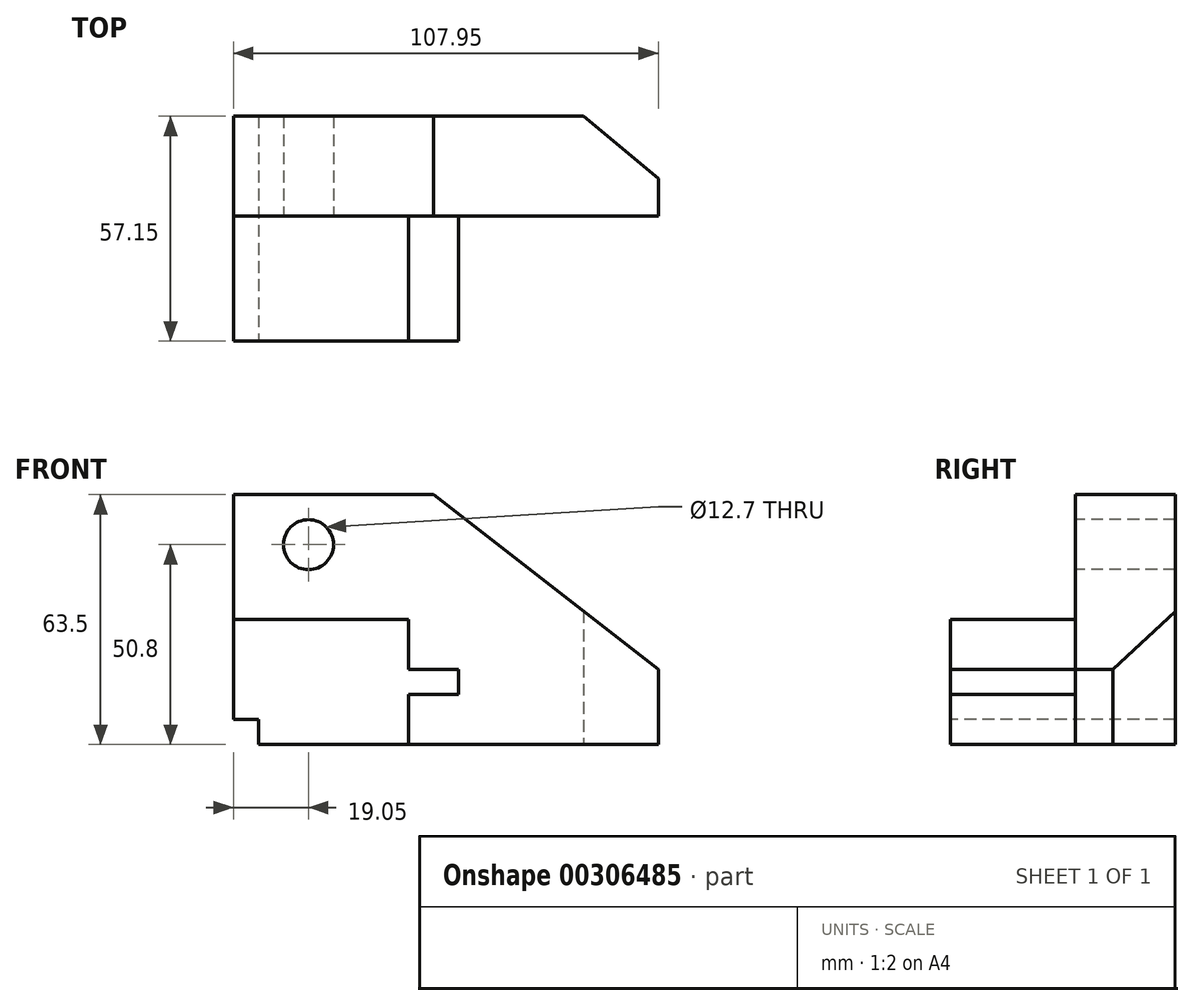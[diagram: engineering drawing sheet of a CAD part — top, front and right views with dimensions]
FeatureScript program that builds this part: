
annotation { "Feature Type Name" : "Feature", "Feature Type Description" : "" }
export const myFeature = defineFeature(function(context is Context, id is Id, definition is map)
    precondition{}
    {
        {
            var Q0;
            Q0=qCreatedBy(makeId("Front.planeOp"),FACE);
            var sketch = newSketch(context, id + "F0", { "sketchPlane" : qUnion([Q0])});
            skLineSegment(sketch, "E0.bottom", {"start": v(0, 0) * mm, "end": v(44.45, 0) * mm});
            skLineSegment(sketch, "E0.top", {"start": v(0, 31.75) * mm, "end": v(44.45, 31.75) * mm});
            skLineSegment(sketch, "E0.left", {"start": v(0, 0) * mm, "end": v(0, 31.75) * mm});
            skLineSegment(sketch, "E0.right", {"start": v(44.45, 0) * mm, "end": v(44.45, 12.7) * mm});
            skLineSegment(sketch, "E1.bottom", {"start": v(44.45, 19.05) * mm, "end": v(57.15, 19.05) * mm});
            skLineSegment(sketch, "E1.top", {"start": v(44.45, 12.7) * mm, "end": v(57.15, 12.7) * mm});
            skLineSegment(sketch, "E1.right", {"start": v(57.15, 19.05) * mm, "end": v(57.15, 12.7) * mm});
            skLineSegment(sketch, "E2.trimOffspring", {"start": v(44.45, 19.05) * mm, "end": v(44.45, 31.75) * mm});
            skSolve(sketch);
        }
        {
            var Q0;
            Q0 = qSketchRegion(id + "F0", true);
            extrude(context, id + "F1", {"entities" : qUnion([Q0]), "depth" : 31.75 * mm});
        }
        {
            var Q0;
            Q0=qCreatedBy(makeId("Front.planeOp"),FACE);
            var sketch = newSketch(context, id + "F2", { "sketchPlane" : qUnion([Q0])});
            skLineSegment(sketch, "E3.bottom", {"start": v(0, 0) * mm, "end": v(107.95, 0) * mm});
            skLineSegment(sketch, "E3.top", {"start": v(0, 63.5) * mm, "end": v(50.8, 63.5) * mm});
            skLineSegment(sketch, "E3.left", {"start": v(0, 0) * mm, "end": v(0, 63.5) * mm});
            skLineSegment(sketch, "E3.right", {"start": v(107.95, 0) * mm, "end": v(107.95, 19.05) * mm});
            skLineSegment(sketch, "E4", {"start": v(50.8, 63.5) * mm, "end": v(107.95, 19.05) * mm});
            skCircle(sketch, "E5", {"center": v(19.05, 50.8) * mm, "radius": 6.35 * mm});
            skSolve(sketch);
        }
        {
            var Q0;
            Q0 = qSketchRegion(id + "F2", true);
            extrude(context, id + "F3", {"entities" : qUnion([Q0]), "operationType" : NewBodyOperationType.ADD, "oppositeDirection" : true, "depth" : 25.4 * mm});
        }
        {
            var Q0;
            Q0=qCreatedBy(makeId("Top.planeOp"),FACE);
            var sketch = newSketch(context, id + "F4", { "sketchPlane" : qUnion([Q0])});
            skLineSegment(sketch, "E6", {"start": v(88.9, 25.4) * mm, "end": v(107.95, 9.52) * mm});
            skLineSegment(sketch, "E7", {"start": v(107.95, 9.53) * mm, "end": v(107.95, 25.4) * mm});
            skLineSegment(sketch, "E8", {"start": v(107.95, 25.4) * mm, "end": v(88.9, 25.4) * mm});
            skSolve(sketch);
        }
        {
            var Q0;
            Q0 = qSketchRegion(id + "F4", true);
            extrude(context, id + "F5", {"entities" : qUnion([Q0]), "operationType" : NewBodyOperationType.REMOVE, "endBound" : BoundingType.THROUGH_ALL, "depth" : 25.4 * mm});
        }
        {
            var Q0;
            Q0=makeQuery(id+"F1.opExtrude","CAP_FACE",FACE,{"disambiguationData":[OSD([sQuery(id+"F0.wireOp",EDGE,"E0.bottom"),sQuery(id+"F0.wireOp",EDGE,"E0.top"),sQuery(id+"F0.wireOp",EDGE,"E0.left"),sQuery(id+"F0.wireOp",EDGE,"E0.right"),sQuery(id+"F0.wireOp",EDGE,"E1.bottom"),sQuery(id+"F0.wireOp",EDGE,"E1.top"),sQuery(id+"F0.wireOp",EDGE,"E1.right"),sQuery(id+"F0.wireOp",EDGE,"E2.trimOffspring")])],"isStart":false});
            var sketch = newSketch(context, id + "F6", { "sketchPlane" : qUnion([Q0])});
            skLineSegment(sketch, "E9.bottom", {"start": v(0, 0) * mm, "end": v(6.35, 0) * mm});
            skLineSegment(sketch, "E9.top", {"start": v(0, 6.35) * mm, "end": v(6.35, 6.35) * mm});
            skLineSegment(sketch, "E9.left", {"start": v(0, 0) * mm, "end": v(0, 6.35) * mm});
            skLineSegment(sketch, "E9.right", {"start": v(6.35, 0) * mm, "end": v(6.35, 6.35) * mm});
            skSolve(sketch);
        }
        {
            var Q0;
            Q0 = qSketchRegion(id + "F6", true);
            extrude(context, id + "F7", {"entities" : qUnion([Q0]), "operationType" : NewBodyOperationType.REMOVE, "endBound" : BoundingType.THROUGH_ALL, "oppositeDirection" : true, "depth" : 25.4 * mm});
        }
    });
